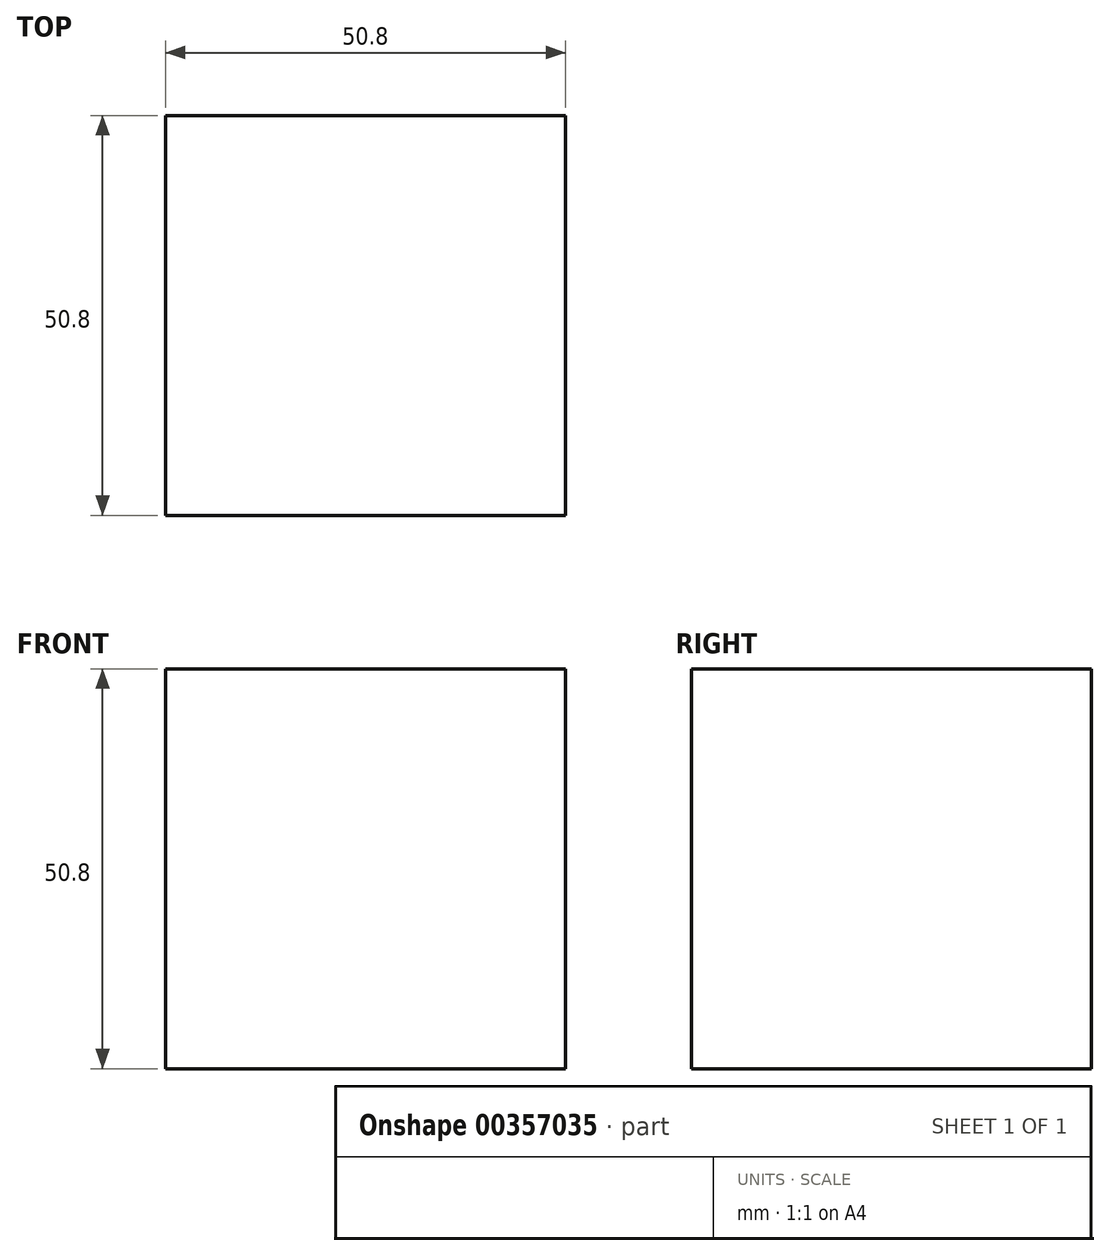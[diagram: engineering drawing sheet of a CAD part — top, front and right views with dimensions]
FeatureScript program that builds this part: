
annotation { "Feature Type Name" : "Feature", "Feature Type Description" : "" }
export const myFeature = defineFeature(function(context is Context, id is Id, definition is map)
    precondition{}
    {
        {
            var Q0;
            Q0=qCreatedBy(makeId("Front.planeOp"),FACE);
            var sketch = newSketch(context, id + "F0", { "sketchPlane" : qUnion([Q0])});
            skLineSegment(sketch, "E0", {"start": v(0, 0) * mm, "end": v(50.8, 0) * mm});
            skLineSegment(sketch, "E1", {"start": v(50.8, 0) * mm, "end": v(50.8, 50.8) * mm});
            skLineSegment(sketch, "E2", {"start": v(50.8, 50.8) * mm, "end": v(0, 50.8) * mm});
            skLineSegment(sketch, "E3", {"start": v(0, 50.8) * mm, "end": v(0, 0) * mm});
            skSolve(sketch);
        }
        {
            var Q0;
            Q0 = qSketchRegion(id + "F0", true);
            extrude(context, id + "F1", {"entities" : qUnion([Q0]), "depth" : 50.8 * mm});
        }
    });
